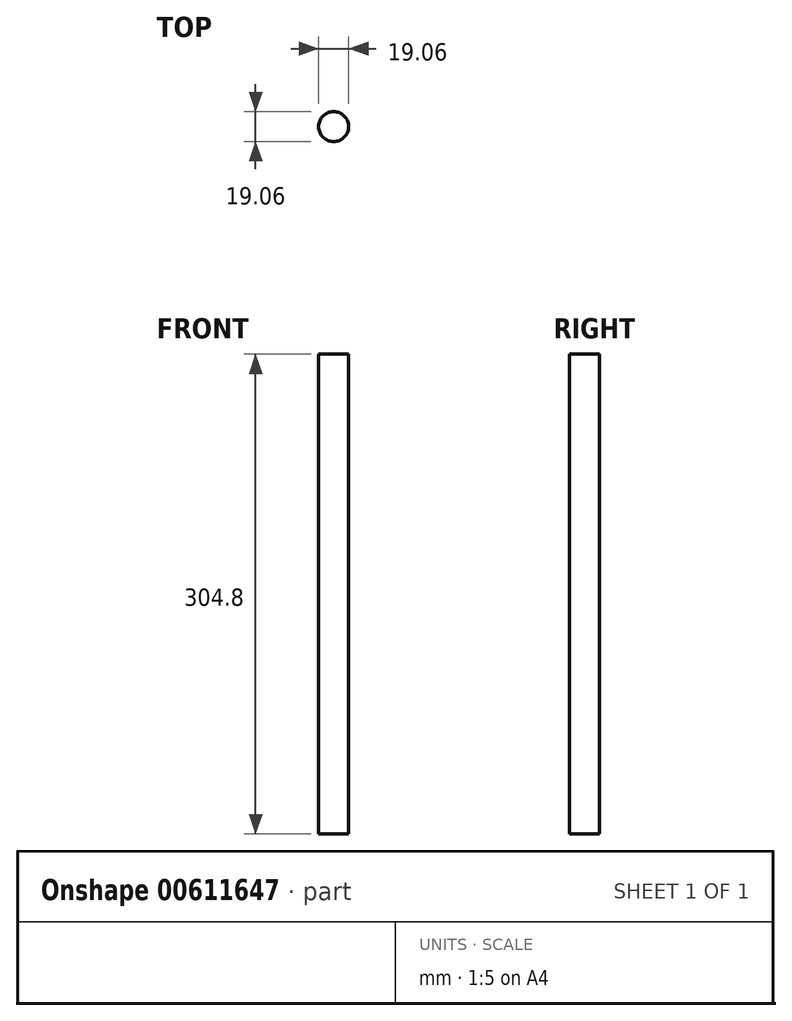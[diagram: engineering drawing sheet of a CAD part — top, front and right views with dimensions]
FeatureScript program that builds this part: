
annotation { "Feature Type Name" : "Feature", "Feature Type Description" : "" }
export const myFeature = defineFeature(function(context is Context, id is Id, definition is map)
    precondition{}
    {
        {
            var Q0;
            Q0=qCreatedBy(makeId("Top.planeOp"),FACE);
            var sketch = newSketch(context, id + "F0", { "sketchPlane" : qUnion([Q0])});
            skCircle(sketch, "E0", {"center": v(0, 0) * mm, "radius": 9.53 * mm});
            skSolve(sketch);
        }
        {
            var Q0;
            Q0=makeQuery(id+"F0.imprint","IMPRINT",FACE,{"disambiguationData":[TD([[makeQuery(id+"F0.imprint","IMPRINT",EDGE,{"derivedFrom":sQuery(id+"F0.wireOp",EDGE,"E0")}),1.0]])]});
            extrude(context, id + "F1", {"entities" : qUnion([Q0]), "depth" : 304.8 * mm, "offsetDistance" : 25.4 * mm});
        }
    });
